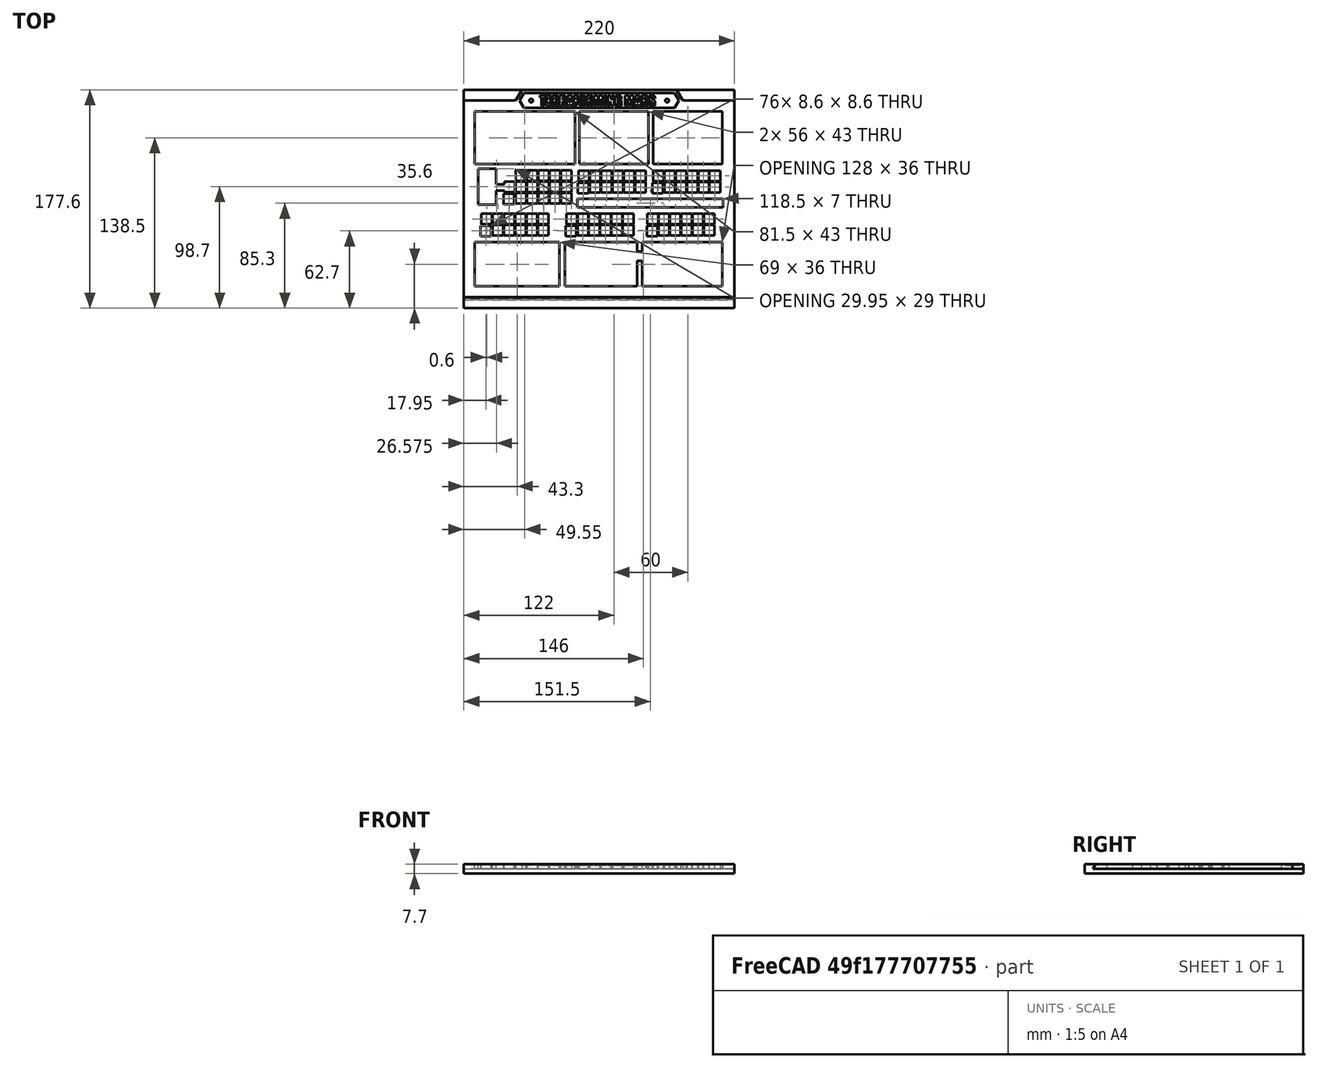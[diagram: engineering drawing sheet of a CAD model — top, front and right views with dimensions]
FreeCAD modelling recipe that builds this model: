
FCSTD DOCUMENT  (FreeCAD 0.21R33668 +26 (Git))
Label: overlay-full-v3
License: All rights reserved
LicenseURL: https://en.wikipedia.org/wiki/All_rights_reserved
objects: Sketcher::SketchObject×8, PartDesign::Pad×8, PartDesign::Pocket×3, Part::Feature×2, PartDesign::Body×2, Mesh::Feature×1, Part::Refine×1, PartDesign::FeatureBase×1, Part::Part2DObjectPython×1, Part::Extrusion×1
note: 38 computed .brp shape members not serialized (recipe doc carries the construction recipe); baked Part::Feature solids carry a one-line shape summary decoded from their .brp

FEATURE [Mesh::Feature] Terraforming_Mars_overlay
FEATURE [Part::Feature] Terraforming_Mars_overlay001
  shape: bbox 208 x 148 x 3.7 mm, 1736 faces, 0 solids (baked)
FEATURE [Part::Feature] Terraforming_Mars_overlay001_solid  label="Terraforming_Mars_overlay001 (Solid)"
  shape: bbox 208 x 148 x 3.7 mm, 1736 faces (baked)
FEATURE [Part::Refine] Terraforming_Mars_overlay001_solid001  label="Terraforming_Mars_overlay001 (Solid)001"
  Source = -> Terraforming_Mars_overlay001_solid
FEATURE [PartDesign::FeatureBase] BaseFeature
  BaseFeature = -> Terraforming_Mars_overlay001_solid001
FEATURE [Sketcher::SketchObject] Sketch
  ExternalGeometry = -> [BaseFeature]
  FullyConstrained = true
  MapMode = 5
  Placement = pos=(0,0,3.7) rot=(0,0,1;0rad)
  Support = -> [BaseFeature]
  sketch-geometry (8):
    g0: LineSegment StartX=6 StartY=154 StartZ=0 EndX=214 EndY=154 EndZ=0
    g1: LineSegment StartX=214 StartY=154 StartZ=0 EndX=214 EndY=6 EndZ=0
    g2: LineSegment StartX=214 StartY=6 StartZ=0 EndX=6 EndY=6 EndZ=0
    g3: LineSegment StartX=6 StartY=6 StartZ=0 EndX=6 EndY=154 EndZ=0
    g4: LineSegment StartX=0 StartY=160 StartZ=0 EndX=220 EndY=160 EndZ=0
    g5: LineSegment StartX=220 StartY=160 StartZ=0 EndX=220 EndY=0 EndZ=0
    g6: LineSegment StartX=220 StartY=0 StartZ=0 EndX=0 EndY=0 EndZ=0
    g7: LineSegment StartX=0 StartY=0 StartZ=0 EndX=0 EndY=160 EndZ=0
  constraints (22):
    c: Coincident(g0,g1)
    c: Coincident(g1,g2)
    c: Coincident(g2,g3)
    c: Coincident(g3,g0)
    c: Horizontal(g0)
    c: Horizontal(g2)
    c: Vertical(g1)
    c: Vertical(g3)
    c: Coincident(g0,g-3)
    c: Coincident(g1,g-4)
    c: Coincident(g4,g5)
    c: Coincident(g5,g6)
    c: Coincident(g6,g7)
    c: Coincident(g7,g4)
    c: Horizontal(g4)
    c: Horizontal(g6)
    c: Vertical(g5)
    c: Vertical(g7)
    c: DistanceX(g4,g0) = 6
    c: DistanceX(g0,g4) = 6
    c: DistanceY(g0,g4) = 6
    c: DistanceY(g5,g1) = 6
FEATURE [PartDesign::Pad] Pad
  BaseFeature = -> BaseFeature
  Direction = (0,0,1)
  Length = 10
  Length2 = 10
  Profile = -> Sketch
  ReferenceAxis = -> Sketch [N_Axis]
  Type = 3
  UpToFace = -> BaseFeature [Face1]
FEATURE [Sketcher::SketchObject] Sketch001
  ExternalGeometry = -> [Pad]
  FullyConstrained = true
  MapMode = 5
  Placement = pos=(0,0,3.7) rot=(0,0,1;0rad)
  Support = -> [Pad]
  sketch-geometry (5):
    g0: GeomPoint X=110 Y=160 Z=0
    g1: LineSegment StartX=42 StartY=160 StartZ=0 EndX=47.0807 EndY=168.8 EndZ=0
    g2: LineSegment StartX=47.0807 StartY=168.8 StartZ=0 EndX=172.919 EndY=168.8 EndZ=0
    g3: LineSegment StartX=172.919 StartY=168.8 StartZ=0 EndX=178 EndY=160 EndZ=0
    g4: LineSegment StartX=178 StartY=160 StartZ=0 EndX=42 EndY=160 EndZ=0
  constraints (13):
    c: Symmetric(g-3,g-3,g0)
    c: Coincident(g1,g2)
    c: Horizontal(g2)
    c: Coincident(g2,g3)
    c: Coincident(g3,g4)
    c: Coincident(g4,g1)
    c: Angle(g1,g4,g1) = 2.0944
    c: Angle(g4,g3,g3) = 2.0944
    c: DistanceY(g1,g1) = 8.8
    c: PointOnObject(g1,g-3)
    c: DistanceX(g-3,g1) = 42
    c: DistanceX(g3,g-3) = 42
    c: PointOnObject(g3,g-3)
FEATURE [PartDesign::Pad] Pad001
  BaseFeature = -> Pad
  Direction = (0,0,1)
  Length = 10
  Length2 = 10
  Profile = -> Sketch001
  ReferenceAxis = -> Sketch001 [N_Axis]
  Type = 3
  UpToFace = -> Pad [Face2]
FEATURE [Sketcher::SketchObject] Sketch002
  ExternalGeometry = -> [Pad001]
  FullyConstrained = true
  MapMode = 5
  Placement = pos=(0,0,3.7) rot=(0,0,1;0rad)
  Support = -> [Pad001]
  sketch-geometry (7):
    g0: GeomPoint X=110 Y=160 Z=0
    g1: LineSegment StartX=45.2332 StartY=160 StartZ=0 EndX=48.6973 EndY=166 EndZ=0
    g2: LineSegment StartX=48.6973 StartY=166 StartZ=0 EndX=171.303 EndY=166 EndZ=0
    g3: LineSegment StartX=171.303 StartY=166 StartZ=0 EndX=174.767 EndY=160 EndZ=0
    g4: LineSegment StartX=174.767 StartY=160 StartZ=0 EndX=171.303 EndY=154 EndZ=0
    g5: LineSegment StartX=171.303 StartY=154 StartZ=0 EndX=48.6973 EndY=154 EndZ=0
    g6: LineSegment StartX=48.6973 StartY=154 StartZ=0 EndX=45.2332 EndY=160 EndZ=0
  constraints (17):
    c: Symmetric(g-4,g-4,g0)
    c: PointOnObject(g1,g-4)
    c: Coincident(g1,g2)
    c: Horizontal(g2)
    c: Coincident(g2,g3)
    c: PointOnObject(g3,g-4)
    c: Coincident(g3,g4)
    c: PointOnObject(g4,g-5)
    c: Coincident(g4,g5)
    c: Coincident(g5,g6)
    c: Coincident(g6,g1)
    c: Parallel(g1,g-6)
    c: Symmetric(g5,g1,g-4)
    c: Symmetric(g4,g2,g-4)
    c: Parallel(g3,g-7)
    c: Distance(g1,g-6) = 2.8
    c: Distance(g2,g-7) = 2.8
FEATURE [PartDesign::Pocket] Pocket
  BaseFeature = -> Pad001
  Direction = (0,0,-1)
  Length = 1
  Length2 = 5
  Profile = -> Sketch002
  ReferenceAxis = -> Sketch002 [N_Axis]
  Type = 0
FEATURE [Part::Part2DObjectPython] ShapeString  # Draft 2D object (typed FeaturePython)
  FontFile = <path>
  MakeFace = true
  Placement = pos=(61.7,155.5,2.7) rot=(0,0,1;0rad)
  Size = 9
  String = TERRAFORMING MARS
  Tracking = 0
FEATURE [Sketcher::SketchObject] Sketch003
  ExternalGeometry = -> [Pocket]
  FullyConstrained = true
  MapMode = 5
  Placement = pos=(0,0,2.7) rot=(0,0,1;0rad)
  Support = -> [Pocket]
  sketch-geometry (3):
    g0: LineSegment StartX=45.2332 StartY=160 StartZ=0 EndX=174.767 EndY=160 EndZ=0
    g1: Circle CenterX=54.7332 CenterY=160 CenterZ=0 NormalX=0 NormalY=0 NormalZ=1 AngleXU=0 Radius=1.5
    g2: Circle CenterX=165.267 CenterY=160 CenterZ=0 NormalX=0 NormalY=0 NormalZ=1 AngleXU=0 Radius=1.5
  constraints (8):
    c: Coincident(g0,g-3)
    c: Coincident(g0,g-4)
    c: PointOnObject(g1,g0)
    c: PointOnObject(g2,g0)
    c: Diameter(g2) = 3
    c: Diameter(g1) = 3
    c: DistanceX(g0,g1) = 9.5
    c: DistanceX(g2,g0) = 9.5
FEATURE [PartDesign::Pad] Pad002
  BaseFeature = -> Pocket
  Direction = (0,0,1)
  Length = 1
  Length2 = 10
  Profile = -> Sketch003
  ReferenceAxis = -> Sketch003 [N_Axis]
  Type = 0
FEATURE [PartDesign::Pad] Pad003
  BaseFeature = -> Pad002
  Direction = (0,-1,0)
  Length = 2
  Length2 = 10
  Profile = -> Pad002 [Face352]
  Type = 0
FEATURE [Sketcher::SketchObject] Sketch004
  ExternalGeometry = -> [Pad003]
  FullyConstrained = true
  MapMode = 5
  Placement = pos=(220,0,0) rot=(0.57735,0.57735,0.57735;2.0944rad)
  Support = -> [Pad003]
  sketch-geometry (3):
    g0: LineSegment StartX=0 StartY=3.7 StartZ=0 EndX=-2 EndY=0 EndZ=0
    g1: LineSegment StartX=-2 StartY=0 StartZ=0 EndX=-2 EndY=3.7 EndZ=0
    g2: LineSegment StartX=-2 StartY=3.7 StartZ=0 EndX=0 EndY=3.7 EndZ=0
  constraints (6):
    c: Coincident(g-4,g0)
    c: Coincident(g0,g-3)
    c: Coincident(g0,g1)
    c: Coincident(g1,g-4)
    c: Coincident(g1,g2)
    c: Coincident(g2,g0)
FEATURE [PartDesign::Pocket] Pocket001
  BaseFeature = -> Pad003
  Direction = (-1,0,0)
  Length = 5
  Length2 = 5
  Profile = -> Sketch004
  ReferenceAxis = -> Sketch004 [N_Axis]
  Type = 1
FEATURE [PartDesign::Body] Body  label="Front"
  BaseFeature = -> Terraforming_Mars_overlay001_solid001
  Group = -> [BaseFeature,Sketch,Pad,Sketch001,Pad001,Sketch002,Pocket,Sketch003,Pad002,Pad003,Sketch004,Pocket001]
  Origin = -> Origin
  Tip = -> Pocket001
FEATURE [Part::Extrusion] Extrude  label="Text"
  Base = -> ShapeString
  Dir = (0,0,1)
  DirMode = 2
  FaceMakerClass = Part::FaceMakerBullseye
  LengthFwd = 1
  LengthRev = 0
  Solid = false
  Symmetric = false
FEATURE [Sketcher::SketchObject] Sketch005
  FullyConstrained = true
  MapMode = 5
  Support = -> [XY_Plane001]
  sketch-geometry (4):
    g0: LineSegment StartX=0 StartY=160 StartZ=0 EndX=220 EndY=160 EndZ=0
    g1: LineSegment StartX=220 StartY=160 StartZ=0 EndX=220 EndY=0 EndZ=0
    g2: LineSegment StartX=220 StartY=0 StartZ=0 EndX=0 EndY=0 EndZ=0
    g3: LineSegment StartX=0 StartY=0 StartZ=0 EndX=0 EndY=160 EndZ=0
  constraints (12):
    c: Coincident(g0,g1)
    c: Coincident(g1,g2)
    c: Coincident(g2,g3)
    c: Coincident(g3,g0)
    c: Horizontal(g0)
    c: Horizontal(g2)
    c: Vertical(g1)
    c: Vertical(g3)
    c: PointOnObject(g1,g-1)
    c: PointOnObject(g0,g-2)
    c: DistanceX(g0,g0) = 220
    c: DistanceY(g1,g1) = 160
FEATURE [PartDesign::Pad] Pad004
  Direction = (0,0,1)
  Length = 4
  Length2 = 10
  Profile = -> Sketch005
  ReferenceAxis = -> Sketch005 [N_Axis]
  Reversed = true
  Type = 0
FEATURE [PartDesign::Pad] Pad005
  BaseFeature = -> Pad004
  Direction = (0,-1,0)
  Length = 8.8
  Length2 = 10
  Profile = -> Pad004 [Face3]
  Type = 0
FEATURE [PartDesign::Pad] Pad006
  BaseFeature = -> Pad005
  Direction = (0,0,1)
  Length = 3.7
  Length2 = 10
  Profile = -> Pad005 [Face8]
  Type = 0
FEATURE [Sketcher::SketchObject] Sketch006
  ExternalGeometry = -> [Pad006]
  FullyConstrained = true
  MapMode = 5
  Placement = pos=(0,0,0) rot=(0.57735,-0.57735,-0.57735;2.0944rad)
  Support = -> [Pad006]
  sketch-geometry (4):
    g0: LineSegment StartX=0 StartY=0 StartZ=0 EndX=2.1 EndY=0 EndZ=0
    g1: LineSegment StartX=0.1 StartY=3.7 StartZ=0 EndX=2.1 EndY=0 EndZ=0
    g2: LineSegment StartX=0 StartY=3.7 StartZ=0 EndX=0 EndY=0 EndZ=0
    g3: LineSegment StartX=0.1 StartY=3.7 StartZ=0 EndX=0 EndY=3.7 EndZ=0
  constraints (10):
    c: Coincident(g-1,g0)
    c: PointOnObject(g0,g-1)
    c: Coincident(g1,g0)
    c: DistanceX(g0,g0) = 2.1
    c: PointOnObject(g1,g-3)
    c: Coincident(g2,g-3)
    c: Coincident(g2,g0)
    c: Coincident(g3,g1)
    c: Coincident(g3,g2)
    c: DistanceX(g3,g3) = 0.1
FEATURE [PartDesign::Pocket] Pocket002
  BaseFeature = -> Pad006
  Direction = (1,0,0)
  Length = 5
  Length2 = 5
  Profile = -> Sketch006
  ReferenceAxis = -> Sketch006 [N_Axis]
  Type = 1
FEATURE [PartDesign::Pad] Pad007
  BaseFeature = -> Pocket002
  Direction = (0,1,0)
  Length = 8.8
  Length2 = 10
  Profile = -> Pocket002 [Face1]
  Type = 0
FEATURE [Sketcher::SketchObject] Sketch007
  ExternalGeometry = -> [Pad007]
  FullyConstrained = true
  MapMode = 5
  Placement = pos=(0,0,0) rot=(0.57735,-0.57735,-0.57735;2.0944rad)
  Support = -> [Pad007]
  sketch-geometry (3):
    g0: LineSegment StartX=4.63784 StartY=3.7 StartZ=0 EndX=8.8 EndY=-4 EndZ=0
    g1: LineSegment StartX=8.8 StartY=-4 StartZ=0 EndX=8.8 EndY=3.7 EndZ=0
    g2: LineSegment StartX=8.8 StartY=3.7 StartZ=0 EndX=4.63784 EndY=3.7 EndZ=0
  constraints (7):
    c: PointOnObject(g0,g-3)
    c: Coincident(g0,g-6)
    c: Coincident(g1,g0)
    c: Coincident(g1,g-5)
    c: Coincident(g2,g1)
    c: Coincident(g2,g0)
    c: Parallel(g0,g-4)
FEATURE [PartDesign::Body] Body001  label="Back"
  Group = -> [Sketch005,Pad004,Pad005,Pad006,Sketch006,Pocket002,Pad007,Sketch007]
  Origin = -> Origin001
  Tip = -> Pad007
note: 1 file-system path scrubbed to <path> (originals preserved in the JSON sidecar)
